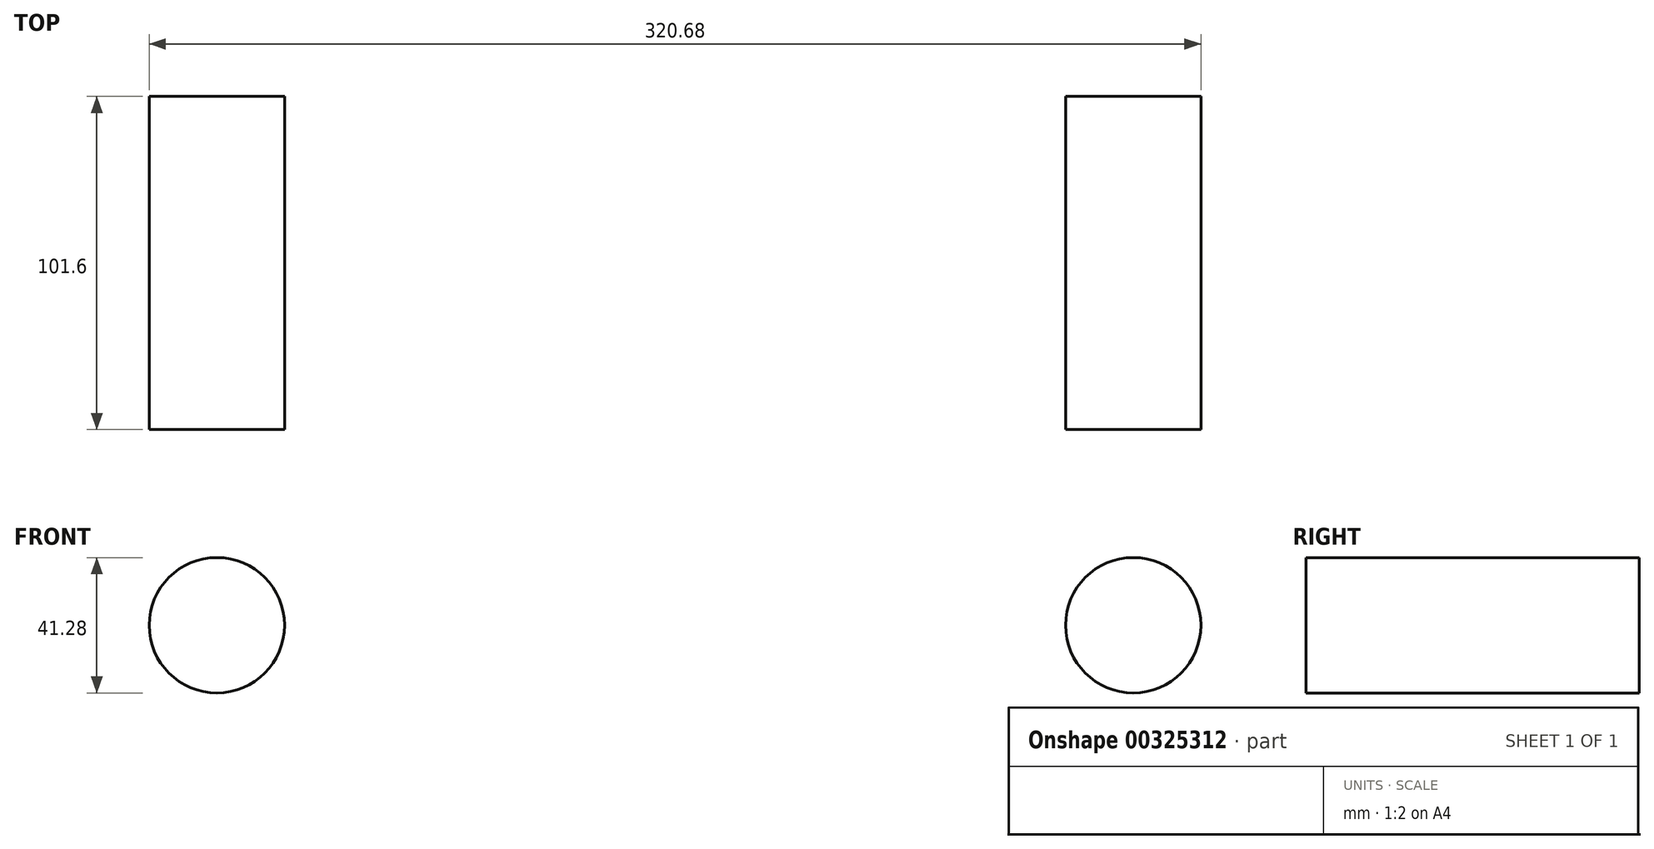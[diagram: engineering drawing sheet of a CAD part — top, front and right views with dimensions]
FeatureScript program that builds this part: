
annotation { "Feature Type Name" : "Feature", "Feature Type Description" : "" }
export const myFeature = defineFeature(function(context is Context, id is Id, definition is map)
    precondition{}
    {
        {
            var Q0;
            Q0=qCreatedBy(makeId("Top.planeOp"),FACE);
            var sketch = newSketch(context, id + "F0", { "sketchPlane" : qUnion([Q0])});
            skLineSegment(sketch, "E0", {"start": v(279.4, -101.6) * mm, "end": v(279.4, 0) * mm});
            skLineSegment(sketch, "E1", {"start": v(0, -101.6) * mm, "end": v(0, 0) * mm});
            skLineSegment(sketch, "E2.bottom", {"start": v(33.02, 67.89) * mm, "end": v(248.92, 67.89) * mm});
            skLineSegment(sketch, "E2.top", {"start": v(33.02, -114.3) * mm, "end": v(248.92, -114.3) * mm});
            skLineSegment(sketch, "E2.left", {"start": v(33.02, 67.89) * mm, "end": v(33.02, -114.3) * mm});
            skLineSegment(sketch, "E2.right", {"start": v(248.92, 67.89) * mm, "end": v(248.92, -114.3) * mm});
            skLineSegment(sketch, "E3.bottom", {"start": v(77.47, -381) * mm, "end": v(204.47, -381) * mm});
            skLineSegment(sketch, "E3.top", {"start": v(77.47, -549.3) * mm, "end": v(204.47, -549.3) * mm});
            skLineSegment(sketch, "E3.left", {"start": v(77.47, -381) * mm, "end": v(77.47, -549.3) * mm});
            skLineSegment(sketch, "E3.right", {"start": v(204.47, -381) * mm, "end": v(204.47, -549.3) * mm});
            skArc(sketch, "E4", {"start": v(279.4, -101.6) * mm, "mid": v(274.57, -125.9) * mm, "end": v(260.8, -146.5) * mm});
            skLineSegment(sketch, "E5", {"start": v(260.8, -146.5) * mm, "end": v(139.47, -267.87) * mm});
            skLineSegment(sketch, "E6", {"start": v(89.56, -292.1) * mm, "end": v(63.5, -292.1) * mm});
            skArc(sketch, "E7", {"start": v(63.5, -292.1) * mm, "mid": v(18.6, -310.7) * mm, "end": v(0, -355.6) * mm});
            skArc(sketch, "E8", {"start": v(0, -101.6) * mm, "mid": v(18.6, -146.5) * mm, "end": v(63.5, -165.1) * mm});
            skLineSegment(sketch, "E9", {"start": v(63.5, -165.1) * mm, "end": v(89.56, -165.1) * mm});
            skArc(sketch, "E10", {"start": v(89.56, -165.1) * mm, "mid": v(153.06, -228.6) * mm, "end": v(89.56, -292.1) * mm});
            skLineSegment(sketch, "E11", {"start": v(0, -355.6) * mm, "end": v(0, -430.49) * mm});
            skPoint(sketch, "E12", {"position": v(140.97, 67.89) * mm});
            skPoint(sketch, "E13", {"position": v(140.97, -549.3) * mm});
            skLineSegment(sketch, "E14.bottom", {"start": v(-19.05, 53.76) * mm, "end": v(19.05, 53.76) * mm});
            skLineSegment(sketch, "E14.top", {"start": v(-19.05, -50.8) * mm, "end": v(19.05, -50.8) * mm});
            skLineSegment(sketch, "E14.left", {"start": v(-19.05, 53.76) * mm, "end": v(-19.05, -50.8) * mm});
            skLineSegment(sketch, "E14.right", {"start": v(19.05, 53.76) * mm, "end": v(19.05, -50.8) * mm});
            skPoint(sketch, "E15", {"position": v(0, 53.76) * mm});
            skLineSegment(sketch, "E16.bottom", {"start": v(260.35, 52.8) * mm, "end": v(298.45, 52.8) * mm});
            skLineSegment(sketch, "E16.top", {"start": v(260.35, -38.1) * mm, "end": v(298.45, -38.1) * mm});
            skLineSegment(sketch, "E16.left", {"start": v(260.35, 52.8) * mm, "end": v(260.35, -38.1) * mm});
            skLineSegment(sketch, "E16.right", {"start": v(298.45, 52.8) * mm, "end": v(298.45, -38.1) * mm});
            skPoint(sketch, "E17", {"position": v(279.4, 52.8) * mm});
            skSolve(sketch);
        }
        {
            var Q0;
            Q0=qCreatedBy(makeId("Front.planeOp"),FACE);
            var sketch = newSketch(context, id + "F1", { "sketchPlane" : qUnion([Q0])});
            skCircle(sketch, "E18", {"center": v(279.4, 0) * mm, "radius": 20.64 * mm});
            skCircle(sketch, "E19", {"center": v(0, 0) * mm, "radius": 20.64 * mm});
            skSolve(sketch);
        }
        {
            var Q0;
            Q0=qSketchRegion(id+"F1",true);
            var Q1;
            Q1=sQuery(id+"F1.wireOp",EDGE,"E18");
            var Q2;
            Q2=sQuery(id+"F0.wireOp",EDGE,"E0");
            sweep(context, id + "F2", {"bodyType" : ToolBodyType.SURFACE, "profiles" : qUnion([Q0]), "surfaceProfiles" : qUnion([Q1]), "path" : qUnion([Q2])});
        }
        {
            var Q0;
            Q0=qSketchRegion(id+"F1",true);
            var Q1;
            Q1=sQuery(id+"F1.wireOp",EDGE,"E19");
            var Q2;
            Q2=sQuery(id+"F0.wireOp",EDGE,"E1");
            sweep(context, id + "F3", {"bodyType" : ToolBodyType.SURFACE, "profiles" : qUnion([Q0]), "surfaceProfiles" : qUnion([Q1]), "path" : qUnion([Q2])});
        }
    });
